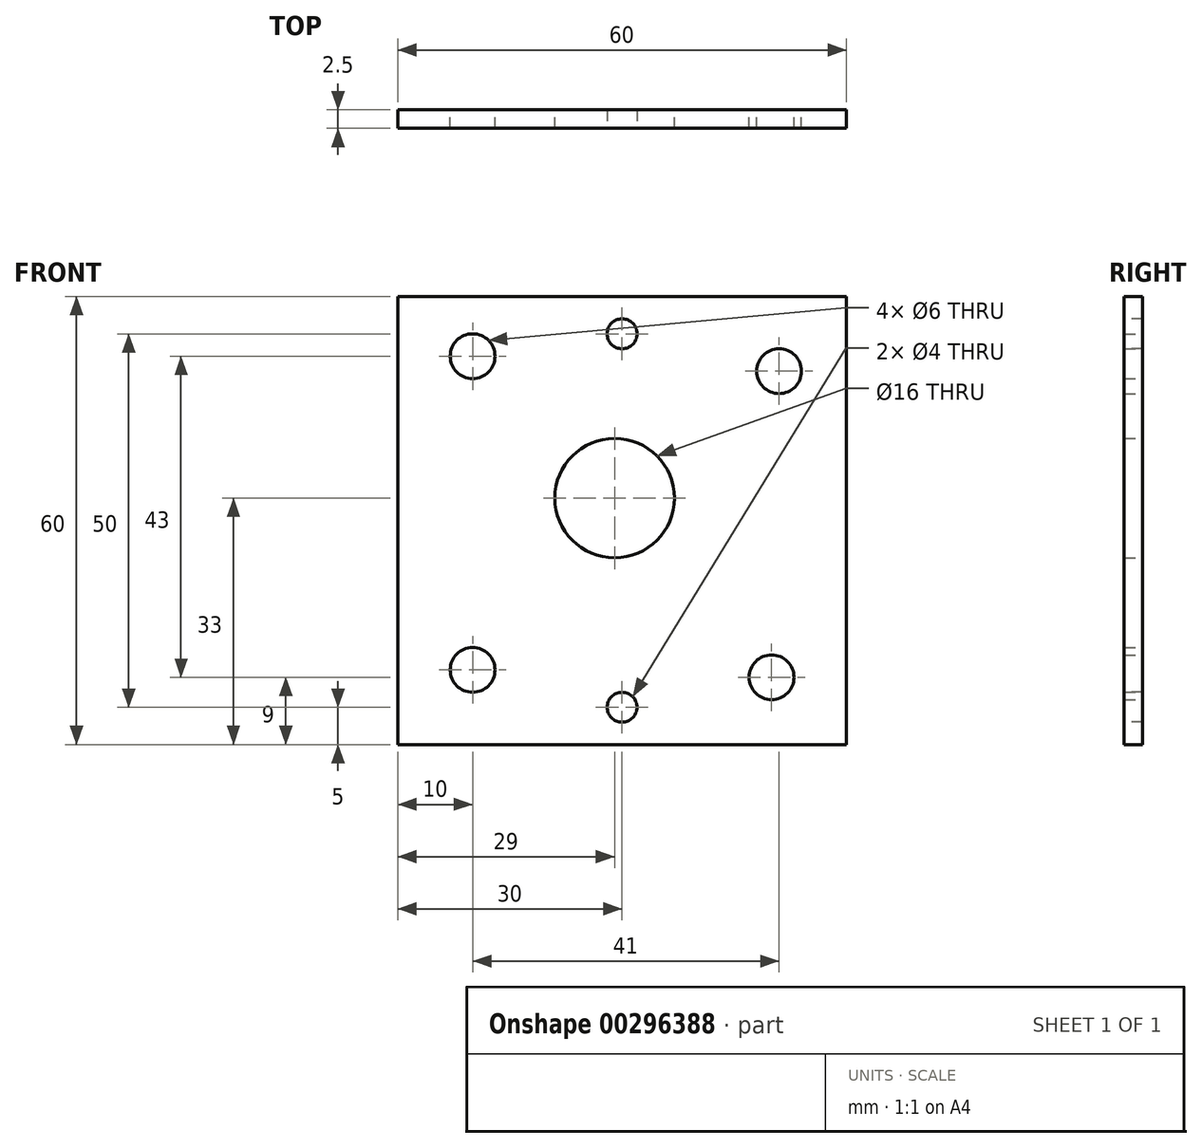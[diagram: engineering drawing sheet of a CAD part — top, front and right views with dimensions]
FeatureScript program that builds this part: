
annotation { "Feature Type Name" : "Feature", "Feature Type Description" : "" }
export const myFeature = defineFeature(function(context is Context, id is Id, definition is map)
    precondition{}
    {
        {
            var Q0;
            Q0=qCreatedBy(makeId("Front.planeOp"),FACE);
            var sketch = newSketch(context, id + "F0", { "sketchPlane" : qUnion([Q0])});
            skLineSegment(sketch, "E0.bottom", {"start": v(-30, 30) * mm, "end": v(30, 30) * mm});
            skLineSegment(sketch, "E0.top", {"start": v(-30, -30) * mm, "end": v(30, -30) * mm});
            skLineSegment(sketch, "E0.left", {"start": v(-30, 30) * mm, "end": v(-30, -30) * mm});
            skLineSegment(sketch, "E0.right", {"start": v(30, 30) * mm, "end": v(30, -30) * mm});
            skPoint(sketch, "E0.middle", {"position": v(0, 0) * mm});
            skCircle(sketch, "E1", {"center": v(-1, 3) * mm, "radius": 8 * mm});
            skCircle(sketch, "E2", {"center": v(-20, 22) * mm, "radius": 3 * mm});
            skCircle(sketch, "E3", {"center": v(-20, -20) * mm, "radius": 3 * mm});
            skCircle(sketch, "E4", {"center": v(21, 20) * mm, "radius": 3 * mm});
            skCircle(sketch, "E5", {"center": v(20, -21) * mm, "radius": 3 * mm});
            skSolve(sketch);
        }
        {
            var Q0;
            Q0=makeQuery(id+"F0.imprint","IMPRINT",FACE,{"disambiguationData":[TD([[makeQuery(id+"F0.imprint","IMPRINT",EDGE,{"derivedFrom":sQuery(id+"F0.wireOp",EDGE,"E0.bottom")}),-1.0]])]});
            extrude(context, id + "F1", {"entities" : qUnion([Q0]), "depth" : 2.5 * mm});
        }
        {
            var Q0;
            Q0=makeQuery(id+"F1.opExtrude","CAP_FACE",FACE,{"disambiguationData":[OSD([sQuery(id+"F0.wireOp",EDGE,"E0.bottom"),sQuery(id+"F0.wireOp",EDGE,"E0.top"),sQuery(id+"F0.wireOp",EDGE,"E0.left"),sQuery(id+"F0.wireOp",EDGE,"E0.right"),sQuery(id+"F0.wireOp",EDGE,"E1"),sQuery(id+"F0.wireOp",EDGE,"E2"),sQuery(id+"F0.wireOp",EDGE,"E3"),sQuery(id+"F0.wireOp",EDGE,"E4"),sQuery(id+"F0.wireOp",EDGE,"E5")])],"isStart":false});
            var sketch = newSketch(context, id + "F2", { "sketchPlane" : qUnion([Q0])});
            skSolve(sketch);
        }
        {
            var Q0;
            Q0=makeQuery(id+"F2.imprint","IMPRINT",FACE,{"disambiguationData":[TD([[makeQuery(id+"F2.imprint","IMPRINT",EDGE,{"derivedFrom":makeQuery(id+"F1.opExtrude","CAP_EDGE",EDGE,{"disambiguationData":[OSD([sQuery(id+"F0.wireOp",EDGE,"E0.bottom")])],"isStart":false})}),-1.0]])]});
            var sketch = newSketch(context, id + "F3", { "sketchPlane" : qUnion([Q0])});
            skCircle(sketch, "E6", {"center": v(0, 25) * mm, "radius": 2 * mm});
            skLineSegment(sketch, "E7", {"start": v(0, 30) * mm, "end": v(0, 19.73) * mm, "construction": true});
            skCircle(sketch, "E8", {"center": v(0, -25) * mm, "radius": 2 * mm});
            skSolve(sketch);
        }
        {
            var Q0;
            Q0 = qSketchRegion(id + "F2", true);
            var Q1;
            Q1 = qSketchRegion(id + "F3", true);
            extrude(context, id + "F4", {"entities" : qUnion([Q0, Q1]), "operationType" : NewBodyOperationType.REMOVE, "oppositeDirection" : true, "depth" : 25 * mm});
        }
    });
